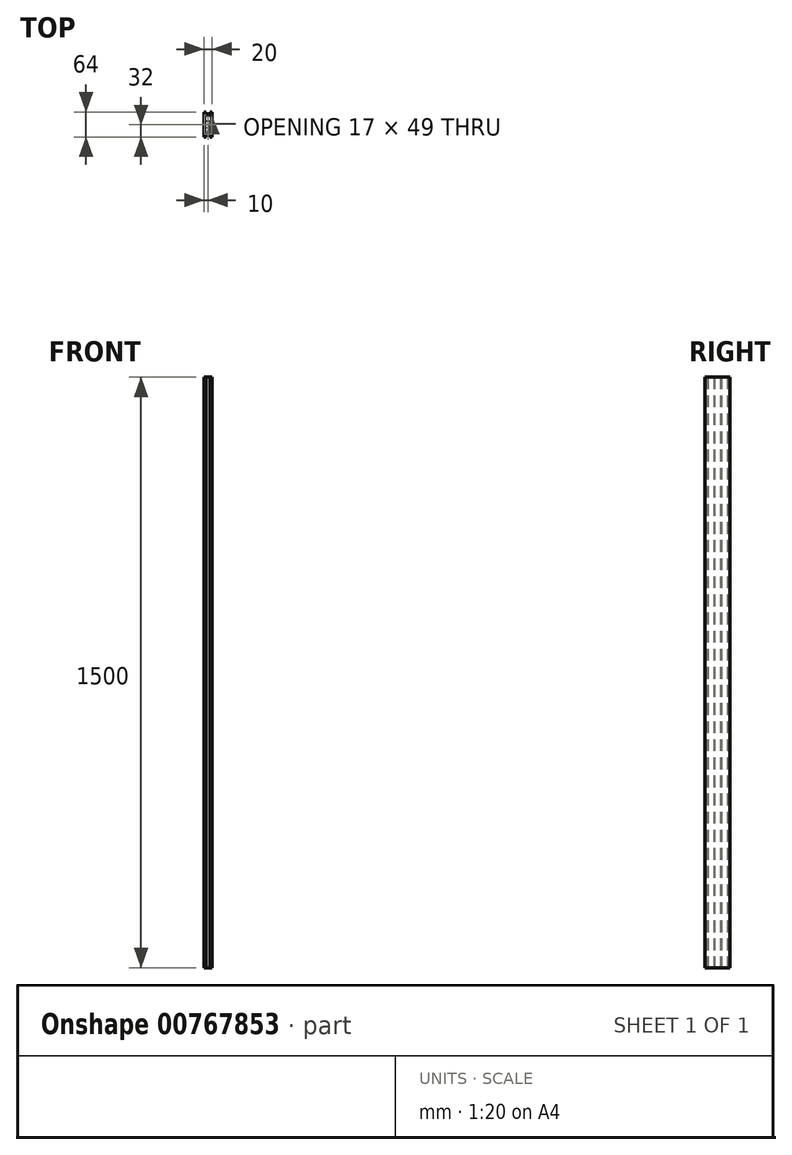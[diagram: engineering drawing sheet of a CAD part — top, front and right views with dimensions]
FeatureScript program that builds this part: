
annotation { "Feature Type Name" : "Feature", "Feature Type Description" : "" }
export const myFeature = defineFeature(function(context is Context, id is Id, definition is map)
    precondition{}
    {
        {
            var Q0;
            Q0=qCreatedBy(makeId("Top.planeOp"),FACE);
            var sketch = newSketch(context, id + "F0", { "sketchPlane" : qUnion([Q0])});
            skLineSegment(sketch, "E0", {"start": v(-5, 32) * mm, "end": v(-10, 32) * mm});
            skLineSegment(sketch, "E1", {"start": v(-10, 32) * mm, "end": v(-10, -32) * mm});
            skLineSegment(sketch, "E2", {"start": v(-10, -32) * mm, "end": v(-5, -32) * mm});
            skLineSegment(sketch, "E3", {"start": v(-5, -32) * mm, "end": v(-5, -30.5) * mm});
            skLineSegment(sketch, "E4", {"start": v(-5, -30.5) * mm, "end": v(-8.5, -30.5) * mm});
            skLineSegment(sketch, "E5", {"start": v(-8.5, -30.5) * mm, "end": v(-8.5, -26) * mm});
            skLineSegment(sketch, "E6", {"start": v(-8.5, -26) * mm, "end": v(8.5, -26) * mm});
            skLineSegment(sketch, "E7", {"start": v(8.5, -26) * mm, "end": v(8.5, -30.5) * mm});
            skLineSegment(sketch, "E8", {"start": v(8.5, -30.5) * mm, "end": v(5, -30.5) * mm});
            skLineSegment(sketch, "E9", {"start": v(5, -30.5) * mm, "end": v(5, -32) * mm});
            skLineSegment(sketch, "E10", {"start": v(5, -32) * mm, "end": v(10, -32) * mm});
            skLineSegment(sketch, "E11", {"start": v(10, -32) * mm, "end": v(10, 32) * mm});
            skLineSegment(sketch, "E12", {"start": v(10, 32) * mm, "end": v(5, 32) * mm});
            skLineSegment(sketch, "E13", {"start": v(5, 32) * mm, "end": v(5, 30.5) * mm});
            skLineSegment(sketch, "E14", {"start": v(5, 30.5) * mm, "end": v(8.5, 30.5) * mm});
            skLineSegment(sketch, "E15", {"start": v(8.5, 30.5) * mm, "end": v(8.5, 26) * mm});
            skLineSegment(sketch, "E16", {"start": v(8.5, 26) * mm, "end": v(-8.5, 26) * mm});
            skLineSegment(sketch, "E17", {"start": v(-8.5, 26) * mm, "end": v(-8.5, 30.5) * mm});
            skLineSegment(sketch, "E18", {"start": v(-8.5, 30.5) * mm, "end": v(-5, 30.5) * mm});
            skLineSegment(sketch, "E19", {"start": v(-5, 30.5) * mm, "end": v(-5, 32) * mm});
            skLineSegment(sketch, "E20", {"start": v(-8.5, 24.5) * mm, "end": v(-8.5, 9.5) * mm});
            skLineSegment(sketch, "E21", {"start": v(-8.5, 9.5) * mm, "end": v(-5.5, 9.5) * mm});
            skLineSegment(sketch, "E22", {"start": v(-5.5, 9.5) * mm, "end": v(-5.5, 7.5) * mm});
            skLineSegment(sketch, "E23", {"start": v(-5.5, 7.5) * mm, "end": v(-8.5, 7.5) * mm});
            skLineSegment(sketch, "E24", {"start": v(-8.5, 7.5) * mm, "end": v(-8.5, -7.5) * mm});
            skLineSegment(sketch, "E25", {"start": v(-8.5, -7.5) * mm, "end": v(-5.5, -7.5) * mm});
            skLineSegment(sketch, "E26", {"start": v(-5.5, -7.5) * mm, "end": v(-5.5, -9.5) * mm});
            skLineSegment(sketch, "E27", {"start": v(-5.5, -9.5) * mm, "end": v(-8.5, -9.5) * mm});
            skLineSegment(sketch, "E28", {"start": v(-8.5, -9.5) * mm, "end": v(-8.5, -24.5) * mm});
            skLineSegment(sketch, "E29", {"start": v(-8.5, -24.5) * mm, "end": v(8.5, -24.5) * mm});
            skLineSegment(sketch, "E30", {"start": v(8.5, -24.5) * mm, "end": v(8.5, -9.5) * mm});
            skLineSegment(sketch, "E31", {"start": v(8.5, -9.5) * mm, "end": v(5.5, -9.5) * mm});
            skLineSegment(sketch, "E32", {"start": v(5.5, -9.5) * mm, "end": v(5.5, -7.5) * mm});
            skLineSegment(sketch, "E33", {"start": v(5.5, -7.5) * mm, "end": v(8.5, -7.5) * mm});
            skLineSegment(sketch, "E34", {"start": v(8.5, -7.5) * mm, "end": v(8.5, 7.5) * mm});
            skLineSegment(sketch, "E35", {"start": v(8.5, 7.5) * mm, "end": v(5.5, 7.5) * mm});
            skLineSegment(sketch, "E36", {"start": v(5.5, 7.5) * mm, "end": v(5.5, 9.5) * mm});
            skLineSegment(sketch, "E37", {"start": v(5.5, 9.5) * mm, "end": v(8.5, 9.5) * mm});
            skLineSegment(sketch, "E38", {"start": v(8.5, 9.5) * mm, "end": v(8.5, 24.5) * mm});
            skLineSegment(sketch, "E39", {"start": v(8.5, 24.5) * mm, "end": v(-8.5, 24.5) * mm});
            skLineSegment(sketch, "E40", {"start": v(0, 26) * mm, "end": v(0, -26) * mm, "construction": true});
            skSolve(sketch);
        }
        {
            var Q0;
            Q0=makeQuery(id+"F0.imprint","IMPRINT",FACE,{"disambiguationData":[TD([[makeQuery(id+"F0.imprint","IMPRINT",EDGE,{"derivedFrom":sQuery(id+"F0.wireOp",EDGE,"E0")}),1.0]])]});
            extrude(context, id + "F1", {"entities" : qUnion([Q0]), "depth" : 1500 * mm, "offsetDistance" : 25 * mm});
        }
    });
